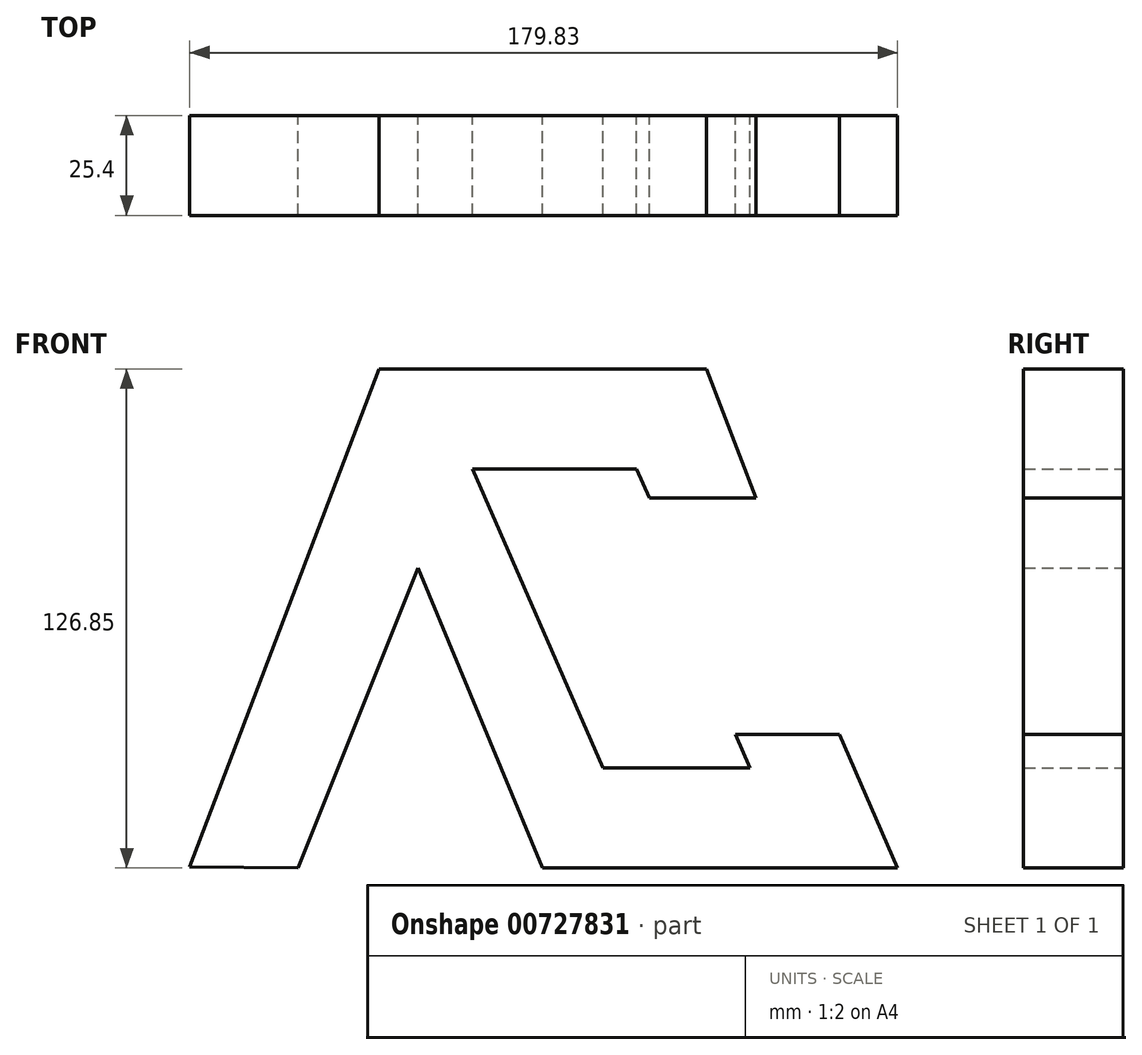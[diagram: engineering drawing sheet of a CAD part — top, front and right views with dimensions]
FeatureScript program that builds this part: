
annotation { "Feature Type Name" : "Feature", "Feature Type Description" : "" }
export const myFeature = defineFeature(function(context is Context, id is Id, definition is map)
    precondition{}
    {
        {
            var Q0;
            Q0=qCreatedBy(makeId("Front.planeOp"),FACE);
            var sketch = newSketch(context, id + "F0", { "sketchPlane" : qUnion([Q0])});
            skLineSegment(sketch, "E0", {"start": v(-89.65, -58.44) * mm, "end": v(-41.64, 68.14) * mm});
            skLineSegment(sketch, "E1", {"start": v(-41.64, 68.14) * mm, "end": v(41.6, 68.14) * mm});
            skLineSegment(sketch, "E2", {"start": v(41.6, 68.14) * mm, "end": v(54.19, 35.3) * mm});
            skLineSegment(sketch, "E3", {"start": v(54.19, 35.3) * mm, "end": v(27.1, 35.3) * mm});
            skLineSegment(sketch, "E4", {"start": v(27.1, 35.3) * mm, "end": v(23.85, 42.74) * mm});
            skLineSegment(sketch, "E5", {"start": v(23.85, 42.74) * mm, "end": v(-17.81, 42.74) * mm});
            skLineSegment(sketch, "E6", {"start": v(-17.81, 42.74) * mm, "end": v(15.32, -33.3) * mm});
            skLineSegment(sketch, "E7", {"start": v(15.32, -33.3) * mm, "end": v(52.66, -33.3) * mm});
            skLineSegment(sketch, "E8", {"start": v(52.66, -33.3) * mm, "end": v(48.94, -24.79) * mm});
            skLineSegment(sketch, "E9", {"start": v(48.94, -24.79) * mm, "end": v(75.37, -24.79) * mm});
            skLineSegment(sketch, "E10", {"start": v(75.37, -24.79) * mm, "end": v(90.18, -58.7) * mm});
            skLineSegment(sketch, "E11", {"start": v(90.18, -58.7) * mm, "end": v(0, -58.7) * mm});
            skLineSegment(sketch, "E12", {"start": v(0, -58.7) * mm, "end": v(-31.67, 17.6) * mm});
            skLineSegment(sketch, "E13", {"start": v(-31.67, 17.6) * mm, "end": v(-62.15, -58.7) * mm});
            skLineSegment(sketch, "E14", {"start": v(-62.15, -58.7) * mm, "end": v(-89.65, -58.44) * mm});
            skSolve(sketch);
        }
        {
            var Q0;
            Q0=makeQuery(id+"F0.imprint","IMPRINT",FACE,{"disambiguationData":[TD([[makeQuery(id+"F0.imprint","IMPRINT",EDGE,{"derivedFrom":sQuery(id+"F0.wireOp",EDGE,"E0")}),-1.0]])]});
            extrude(context, id + "F1", {"entities" : qUnion([Q0]), "endBound" : BoundingType.SYMMETRIC, "depth" : 25.4 * mm, "offsetDistance" : 25.4 * mm});
        }
    });
